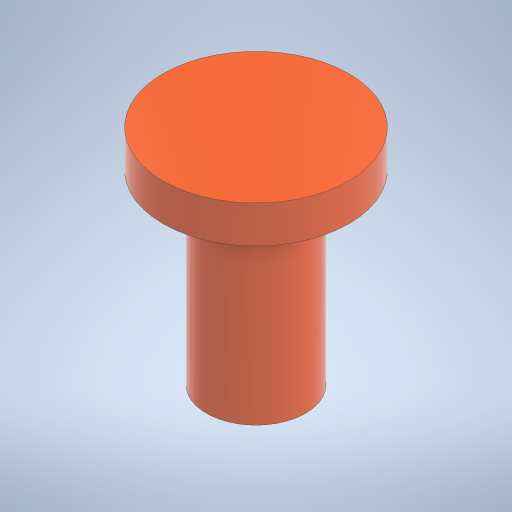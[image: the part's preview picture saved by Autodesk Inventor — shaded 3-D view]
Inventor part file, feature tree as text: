
AUTODESK INVENTOR PART (.ipt)
format: ipt  version: 2024 (Build 280153020, 153B)  size: 227,840 bytes
history: native  units: mm
features: extrude x2, sketch x2
ambient origin geometry x8: Origin, YZ Plane, XZ Plane, XY Plane, X Axis, Y Axis, Z Axis, Center Point
bodies: Solid1 (feature_tree)
feature tree (4):
  extrude  "Extrusion1"  Depth=1.5mm TaperAngle=0.0deg
  extrude  "Extrusion2"  Depth=7.5mm TaperAngle=0.0deg
  sketch  "Sketch1"  dims[d0=7.5mm d1=1.5mm d2=0.0mm]
  sketch  "Sketch2"  dims[d3=4.0mm d4=7.5mm d5=0.0mm]
